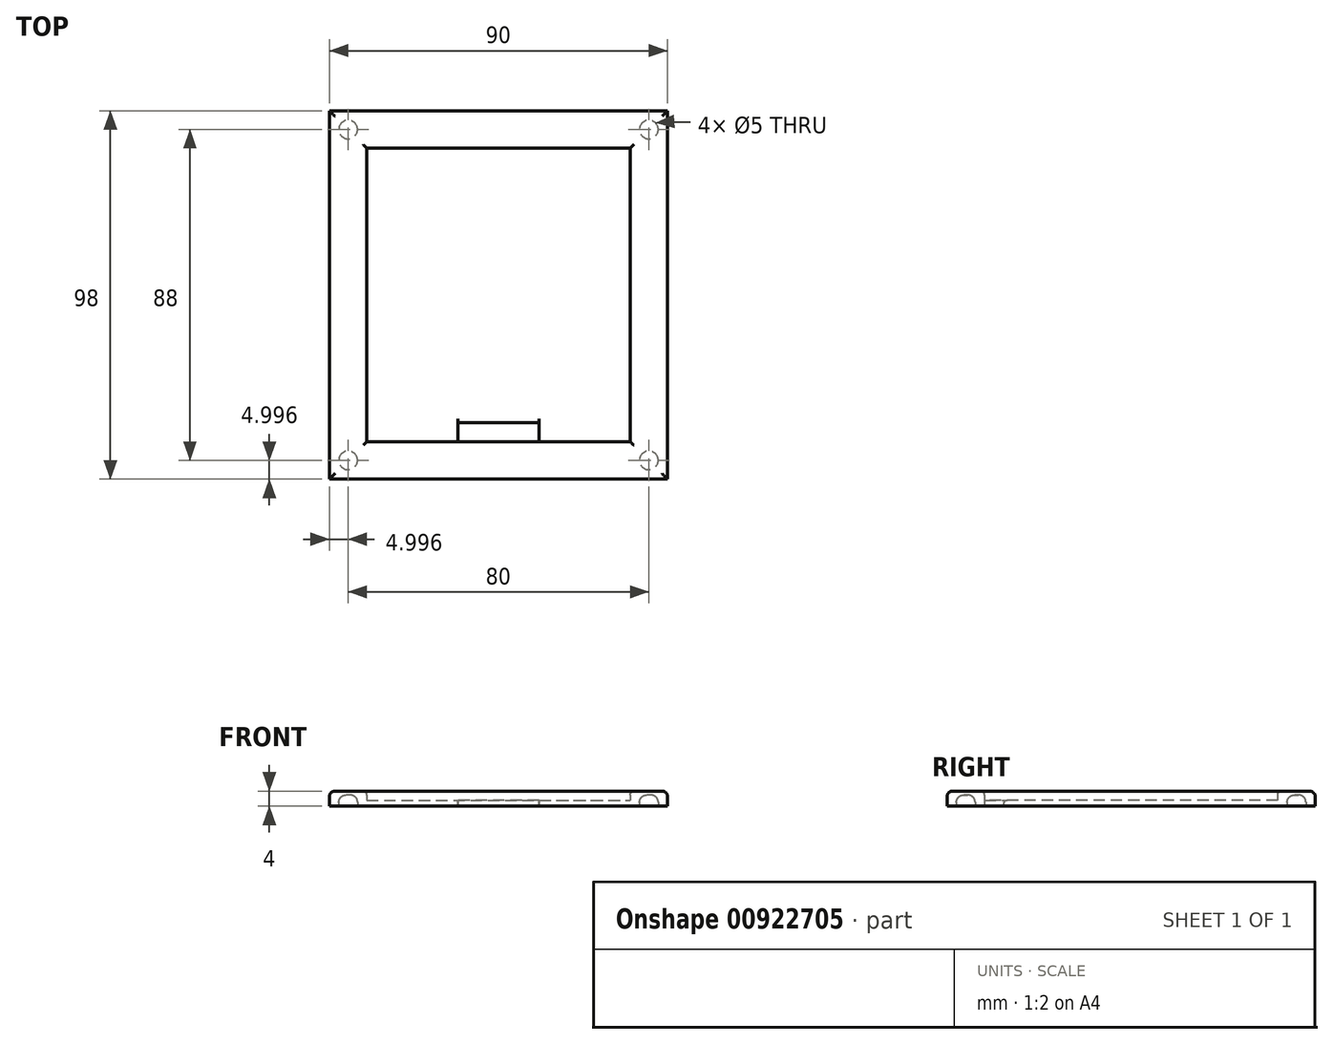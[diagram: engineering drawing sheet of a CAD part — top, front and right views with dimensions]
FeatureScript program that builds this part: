
annotation { "Feature Type Name" : "Feature", "Feature Type Description" : "" }
export const myFeature = defineFeature(function(context is Context, id is Id, definition is map)
    precondition{}
    {
        {
            var Q0;
            Q0=qCreatedBy(makeId("Top.planeOp"),FACE);
            var sketch = newSketch(context, id + "F0", { "sketchPlane" : qUnion([Q0])});
            skLineSegment(sketch, "E0.bottom", {"start": v(-26.62, 40.09) * mm, "end": v(43.38, 40.09) * mm});
            skLineSegment(sketch, "E0.top", {"start": v(-26.62, -37.91) * mm, "end": v(43.38, -37.91) * mm});
            skLineSegment(sketch, "E0.left", {"start": v(-26.62, 40.09) * mm, "end": v(-26.62, -37.91) * mm});
            skLineSegment(sketch, "E0.right", {"start": v(43.38, 40.09) * mm, "end": v(43.38, -37.91) * mm});
            skLineSegment(sketch, "E1.bottom", {"start": v(-36.62, 50.09) * mm, "end": v(53.38, 50.09) * mm});
            skLineSegment(sketch, "E1.top", {"start": v(-36.62, -47.91) * mm, "end": v(53.38, -47.91) * mm});
            skLineSegment(sketch, "E1.left", {"start": v(-36.62, 50.09) * mm, "end": v(-36.62, -47.91) * mm});
            skLineSegment(sketch, "E1.right", {"start": v(53.38, 50.09) * mm, "end": v(53.38, -47.91) * mm});
            skLineSegment(sketch, "E2", {"start": v(0, -47.91) * mm, "end": v(0, -37.91) * mm, "construction": true});
            skLineSegment(sketch, "E3", {"start": v(-36.62, 0) * mm, "end": v(-26.62, 0) * mm, "construction": true});
            skLineSegment(sketch, "E4", {"start": v(8.38, 40.09) * mm, "end": v(8.38, -37.91) * mm, "construction": true});
            skLineSegment(sketch, "E5", {"start": v(-2.37, -37.91) * mm, "end": v(-2.37, -32.91) * mm});
            skLineSegment(sketch, "E6", {"start": v(19.13, -37.91) * mm, "end": v(19.13, -32.91) * mm});
            skLineSegment(sketch, "E7", {"start": v(19.13, -32.91) * mm, "end": v(-2.37, -32.91) * mm});
            skLineSegment(sketch, "E8.bottom", {"start": v(-31.62, 45.09) * mm, "end": v(48.38, 45.09) * mm});
            skLineSegment(sketch, "E8.top", {"start": v(-31.62, -42.91) * mm, "end": v(48.38, -42.91) * mm});
            skLineSegment(sketch, "E8.left", {"start": v(-31.62, 45.09) * mm, "end": v(-31.62, -42.91) * mm});
            skLineSegment(sketch, "E8.right", {"start": v(48.38, 45.09) * mm, "end": v(48.38, -42.91) * mm});
            skCircle(sketch, "E9", {"center": v(-31.62, 45.09) * mm, "radius": 2.5 * mm});
            skCircle(sketch, "E10", {"center": v(48.38, 45.09) * mm, "radius": 2.5 * mm});
            skCircle(sketch, "E11", {"center": v(48.38, -42.91) * mm, "radius": 2.5 * mm});
            skCircle(sketch, "E12", {"center": v(-31.62, -42.91) * mm, "radius": 2.5 * mm});
            skSolve(sketch);
        }
        {
            var Q0;
            Q0=makeQuery(id+"F0.imprint","IMPRINT",FACE,{"disambiguationData":[TD([[makeQuery(id+"F0.imprint","IMPRINT",EDGE,{"derivedFrom":sQuery(id+"F0.wireOp",EDGE,"E0.bottom")}),-1.0]])]});
            extrude(context, id + "F1", {"entities" : qUnion([Q0]), "depth" : 1.5 * mm, "offsetDistance" : 25 * mm});
        }
        {
            var Q0;
            Q0=makeQuery(id+"F0.imprint","IMPRINT",FACE,{"disambiguationData":[TD([[makeQuery(id+"F0.imprint","IMPRINT",EDGE,{"derivedFrom":sQuery(id+"F0.wireOp",EDGE,"E1.bottom")}),-1.0]])]});
            var Q1;
            {var subQ0=sQuery(id+"F0.wireOp",EDGE,"E8.left");var subQ1=sQuery(id+"F0.wireOp",EDGE,"E8.top");var subQ2=makeQuery(id+"F0.imprint","INTERSECT",VERTEX,{"derivedFrom":[subQ1,subQ0]});Q1=makeQuery(id+"F0.imprint","IMPRINT",FACE,{"disambiguationData":[TD([[makeQuery(id+"F0.imprint","IMPRINT",EDGE,{"disambiguationData":[TD([[subQ2,-1.0]])],"derivedFrom":subQ1}),-1.0]])]});}
            var Q2;
            Q2=makeQuery(id+"F0.imprint","IMPRINT",FACE,{"disambiguationData":[TD([[makeQuery(id+"F0.imprint","IMPRINT",EDGE,{"derivedFrom":sQuery(id+"F0.wireOp",EDGE,"E0.bottom")}),1.0]])]});
            var Q3;
            {var subQ0=sQuery(id+"F0.wireOp",EDGE,"E8.left");var subQ1=sQuery(id+"F0.wireOp",EDGE,"E8.top");var subQ2=makeQuery(id+"F0.imprint","INTERSECT",VERTEX,{"derivedFrom":[subQ1,subQ0]});Q3=makeQuery(id+"F0.imprint","IMPRINT",FACE,{"disambiguationData":[TD([[makeQuery(id+"F0.imprint","IMPRINT",EDGE,{"disambiguationData":[TD([[subQ2,-1.0]])],"derivedFrom":subQ1}),1.0]])]});}
            var Q4;
            {var subQ0=sQuery(id+"F0.wireOp",EDGE,"E8.right");var subQ1=sQuery(id+"F0.wireOp",EDGE,"E8.top");var subQ2=makeQuery(id+"F0.imprint","INTERSECT",VERTEX,{"derivedFrom":[subQ1,subQ0]});Q4=makeQuery(id+"F0.imprint","IMPRINT",FACE,{"disambiguationData":[TD([[makeQuery(id+"F0.imprint","IMPRINT",EDGE,{"disambiguationData":[TD([[subQ2,1.0]])],"derivedFrom":subQ1}),-1.0]])]});}
            var Q5;
            {var subQ0=sQuery(id+"F0.wireOp",EDGE,"E8.right");var subQ1=sQuery(id+"F0.wireOp",EDGE,"E8.top");var subQ2=makeQuery(id+"F0.imprint","INTERSECT",VERTEX,{"derivedFrom":[subQ1,subQ0]});Q5=makeQuery(id+"F0.imprint","IMPRINT",FACE,{"disambiguationData":[TD([[makeQuery(id+"F0.imprint","IMPRINT",EDGE,{"disambiguationData":[TD([[subQ2,1.0]])],"derivedFrom":subQ1}),1.0]])]});}
            var Q6;
            {var subQ0=sQuery(id+"F0.wireOp",EDGE,"E8.right");var subQ1=sQuery(id+"F0.wireOp",EDGE,"E8.bottom");var subQ2=makeQuery(id+"F0.imprint","INTERSECT",VERTEX,{"derivedFrom":[subQ1,subQ0]});Q6=makeQuery(id+"F0.imprint","IMPRINT",FACE,{"disambiguationData":[TD([[makeQuery(id+"F0.imprint","IMPRINT",EDGE,{"disambiguationData":[TD([[subQ2,1.0]])],"derivedFrom":subQ1}),-1.0]])]});}
            var Q7;
            {var subQ0=sQuery(id+"F0.wireOp",EDGE,"E8.right");var subQ1=sQuery(id+"F0.wireOp",EDGE,"E8.bottom");var subQ2=makeQuery(id+"F0.imprint","INTERSECT",VERTEX,{"derivedFrom":[subQ1,subQ0]});Q7=makeQuery(id+"F0.imprint","IMPRINT",FACE,{"disambiguationData":[TD([[makeQuery(id+"F0.imprint","IMPRINT",EDGE,{"disambiguationData":[TD([[subQ2,1.0]])],"derivedFrom":subQ1}),1.0]])]});}
            var Q8;
            {var subQ0=sQuery(id+"F0.wireOp",EDGE,"E8.left");var subQ1=sQuery(id+"F0.wireOp",EDGE,"E8.bottom");var subQ2=makeQuery(id+"F0.imprint","INTERSECT",VERTEX,{"derivedFrom":[subQ1,subQ0]});Q8=makeQuery(id+"F0.imprint","IMPRINT",FACE,{"disambiguationData":[TD([[makeQuery(id+"F0.imprint","IMPRINT",EDGE,{"disambiguationData":[TD([[subQ2,-1.0]])],"derivedFrom":subQ1}),1.0]])]});}
            var Q9;
            {var subQ0=sQuery(id+"F0.wireOp",EDGE,"E8.left");var subQ1=sQuery(id+"F0.wireOp",EDGE,"E8.bottom");var subQ2=makeQuery(id+"F0.imprint","INTERSECT",VERTEX,{"derivedFrom":[subQ1,subQ0]});Q9=makeQuery(id+"F0.imprint","IMPRINT",FACE,{"disambiguationData":[TD([[makeQuery(id+"F0.imprint","IMPRINT",EDGE,{"disambiguationData":[TD([[subQ2,-1.0]])],"derivedFrom":subQ1}),-1.0]])]});}
            extrude(context, id + "F2", {"entities" : qUnion([Q0, Q1, Q2, Q3, Q4, Q5, Q6, Q7, Q8, Q9]), "operationType" : NewBodyOperationType.ADD, "depth" : 4 * mm, "offsetDistance" : 25 * mm});
        }
        {
            var Q0;
            Q0=makeQuery(id+"F1.opExtrude","CAP_EDGE",EDGE,{"disambiguationData":[OSD([sQuery(id+"F0.wireOp",EDGE,"E7")])],"isStart":false});
            var Q1;
            Q1=makeQuery(id+"F2.opExtrude","CAP_EDGE",EDGE,{"disambiguationData":[OSD([sQuery(id+"F0.wireOp",EDGE,"E0.left")])],"isStart":false});
            var Q2;
            Q2=makeQuery(id+"F2.opExtrude","CAP_EDGE",EDGE,{"disambiguationData":[OSD([sQuery(id+"F0.wireOp",EDGE,"E0.top")])],"isStart":false});
            var Q3;
            Q3=makeQuery(id+"F2.opExtrude","CAP_EDGE",EDGE,{"disambiguationData":[OSD([sQuery(id+"F0.wireOp",EDGE,"E0.right")])],"isStart":false});
            var Q4;
            Q4=makeQuery(id+"F2.opExtrude","CAP_EDGE",EDGE,{"disambiguationData":[OSD([sQuery(id+"F0.wireOp",EDGE,"E0.bottom")])],"isStart":false});
            fillet(context, id + "F3", {"entities" : qUnion([Q0, Q1, Q2, Q3, Q4]), "radius" : 1 * mm, "tangentPropagation" : true, "allowEdgeOverflow" : false});
        }
        {
            var Q0;
            Q0=makeQuery(id+"F2.opExtrude","CAP_EDGE",EDGE,{"disambiguationData":[OSD([sQuery(id+"F0.wireOp",EDGE,"E1.left")])],"isStart":false});
            var Q1;
            Q1=makeQuery(id+"F2.opExtrude","CAP_EDGE",EDGE,{"disambiguationData":[OSD([sQuery(id+"F0.wireOp",EDGE,"E1.bottom")])],"isStart":false});
            var Q2;
            Q2=makeQuery(id+"F2.opExtrude","CAP_EDGE",EDGE,{"disambiguationData":[OSD([sQuery(id+"F0.wireOp",EDGE,"E1.right")])],"isStart":false});
            var Q3;
            Q3=makeQuery(id+"F2.opExtrude","CAP_EDGE",EDGE,{"disambiguationData":[OSD([sQuery(id+"F0.wireOp",EDGE,"E1.top")])],"isStart":false});
            fillet(context, id + "F4", {"entities" : qUnion([Q0, Q1, Q2, Q3]), "radius" : 1.5 * mm, "tangentPropagation" : true, "allowEdgeOverflow" : false});
        }
        {
            var Q0;
            {var subQ0=sQuery(id+"F0.wireOp",EDGE,"E8.right");var subQ1=sQuery(id+"F0.wireOp",EDGE,"E8.bottom");var subQ2=makeQuery(id+"F0.imprint","INTERSECT",VERTEX,{"derivedFrom":[subQ1,subQ0]});Q0=makeQuery(id+"F0.imprint","IMPRINT",FACE,{"disambiguationData":[TD([[makeQuery(id+"F0.imprint","IMPRINT",EDGE,{"disambiguationData":[TD([[subQ2,1.0]])],"derivedFrom":subQ1}),-1.0]])]});}
            var Q1;
            {var subQ0=sQuery(id+"F0.wireOp",EDGE,"E8.right");var subQ1=sQuery(id+"F0.wireOp",EDGE,"E8.bottom");var subQ2=makeQuery(id+"F0.imprint","INTERSECT",VERTEX,{"derivedFrom":[subQ1,subQ0]});Q1=makeQuery(id+"F0.imprint","IMPRINT",FACE,{"disambiguationData":[TD([[makeQuery(id+"F0.imprint","IMPRINT",EDGE,{"disambiguationData":[TD([[subQ2,1.0]])],"derivedFrom":subQ1}),1.0]])]});}
            var Q2;
            {var subQ0=sQuery(id+"F0.wireOp",EDGE,"E8.left");var subQ1=sQuery(id+"F0.wireOp",EDGE,"E8.bottom");var subQ2=makeQuery(id+"F0.imprint","INTERSECT",VERTEX,{"derivedFrom":[subQ1,subQ0]});Q2=makeQuery(id+"F0.imprint","IMPRINT",FACE,{"disambiguationData":[TD([[makeQuery(id+"F0.imprint","IMPRINT",EDGE,{"disambiguationData":[TD([[subQ2,-1.0]])],"derivedFrom":subQ1}),1.0]])]});}
            var Q3;
            {var subQ0=sQuery(id+"F0.wireOp",EDGE,"E8.left");var subQ1=sQuery(id+"F0.wireOp",EDGE,"E8.bottom");var subQ2=makeQuery(id+"F0.imprint","INTERSECT",VERTEX,{"derivedFrom":[subQ1,subQ0]});Q3=makeQuery(id+"F0.imprint","IMPRINT",FACE,{"disambiguationData":[TD([[makeQuery(id+"F0.imprint","IMPRINT",EDGE,{"disambiguationData":[TD([[subQ2,-1.0]])],"derivedFrom":subQ1}),-1.0]])]});}
            var Q4;
            {var subQ0=sQuery(id+"F0.wireOp",EDGE,"E8.right");var subQ1=sQuery(id+"F0.wireOp",EDGE,"E8.top");var subQ2=makeQuery(id+"F0.imprint","INTERSECT",VERTEX,{"derivedFrom":[subQ1,subQ0]});Q4=makeQuery(id+"F0.imprint","IMPRINT",FACE,{"disambiguationData":[TD([[makeQuery(id+"F0.imprint","IMPRINT",EDGE,{"disambiguationData":[TD([[subQ2,1.0]])],"derivedFrom":subQ1}),1.0]])]});}
            var Q5;
            {var subQ0=sQuery(id+"F0.wireOp",EDGE,"E8.right");var subQ1=sQuery(id+"F0.wireOp",EDGE,"E8.top");var subQ2=makeQuery(id+"F0.imprint","INTERSECT",VERTEX,{"derivedFrom":[subQ1,subQ0]});Q5=makeQuery(id+"F0.imprint","IMPRINT",FACE,{"disambiguationData":[TD([[makeQuery(id+"F0.imprint","IMPRINT",EDGE,{"disambiguationData":[TD([[subQ2,1.0]])],"derivedFrom":subQ1}),-1.0]])]});}
            var Q6;
            {var subQ0=sQuery(id+"F0.wireOp",EDGE,"E8.left");var subQ1=sQuery(id+"F0.wireOp",EDGE,"E8.top");var subQ2=makeQuery(id+"F0.imprint","INTERSECT",VERTEX,{"derivedFrom":[subQ1,subQ0]});Q6=makeQuery(id+"F0.imprint","IMPRINT",FACE,{"disambiguationData":[TD([[makeQuery(id+"F0.imprint","IMPRINT",EDGE,{"disambiguationData":[TD([[subQ2,-1.0]])],"derivedFrom":subQ1}),-1.0]])]});}
            var Q7;
            {var subQ0=sQuery(id+"F0.wireOp",EDGE,"E8.left");var subQ1=sQuery(id+"F0.wireOp",EDGE,"E8.top");var subQ2=makeQuery(id+"F0.imprint","INTERSECT",VERTEX,{"derivedFrom":[subQ1,subQ0]});Q7=makeQuery(id+"F0.imprint","IMPRINT",FACE,{"disambiguationData":[TD([[makeQuery(id+"F0.imprint","IMPRINT",EDGE,{"disambiguationData":[TD([[subQ2,-1.0]])],"derivedFrom":subQ1}),1.0]])]});}
            extrude(context, id + "F5", {"entities" : qUnion([Q0, Q1, Q2, Q3, Q4, Q5, Q6, Q7]), "operationType" : NewBodyOperationType.REMOVE, "depth" : 3 * mm, "offsetDistance" : 25 * mm});
        }
        {
            var Q0;
            Q0=makeQuery(id+"F5.boolean.opBoolean","COPY",EDGE,{"derivedFrom":makeQuery(id+"F5.opExtrude","CAP_EDGE",EDGE,{"disambiguationData":[OSD([sQuery(id+"F0.wireOp",EDGE,"E11")])],"isStart":false})});
            var Q1;
            Q1=makeQuery(id+"F5.boolean.opBoolean","COPY",EDGE,{"derivedFrom":makeQuery(id+"F5.opExtrude","CAP_EDGE",EDGE,{"disambiguationData":[OSD([sQuery(id+"F0.wireOp",EDGE,"E10")])],"isStart":false})});
            var Q2;
            Q2=makeQuery(id+"F5.boolean.opBoolean","COPY",EDGE,{"derivedFrom":makeQuery(id+"F5.opExtrude","CAP_EDGE",EDGE,{"disambiguationData":[OSD([sQuery(id+"F0.wireOp",EDGE,"E9")])],"isStart":false})});
            var Q3;
            Q3=makeQuery(id+"F5.boolean.opBoolean","COPY",EDGE,{"derivedFrom":makeQuery(id+"F5.opExtrude","CAP_EDGE",EDGE,{"disambiguationData":[OSD([sQuery(id+"F0.wireOp",EDGE,"E12")])],"isStart":false})});
            fillet(context, id + "F6", {"entities" : qUnion([Q0, Q1, Q2, Q3]), "radius" : 2 * mm, "tangentPropagation" : true, "allowEdgeOverflow" : false});
        }
    });
